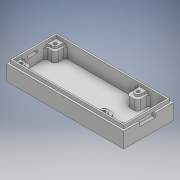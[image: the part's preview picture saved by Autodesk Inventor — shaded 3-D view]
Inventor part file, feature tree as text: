
AUTODESK INVENTOR PART (.ipt)
format: ipt  version: 2018 (Build 220112000, 112)  size: 821,760 bytes
history: native  units: mm
features: extrude x15, sketch x15, projected_geometry x6, other x1, hole x1
ambient origin geometry x8: Origin, YZ Plane, XZ Plane, XY Plane, X Axis, Y Axis, Z Axis, Center Point
bodies: Solid1 (feature_tree)
feature tree (38):
  other  "bottom"
  extrude  "walls"  Depth=3.0mm
  hole  "holes"  [1 undecoded]
  extrude  "tip"  Depth=31.0mm
  extrude  "uart"  Depth=5.0mm
  extrude  "standoffs"  Depth=2.0mm
  extrude  "finalStandoff"  Depth=2.0mm TaperAngle=0.0deg
  extrude  "forNuts"  Depth=100.0mm
  extrude  "mountHoles"  Depth=10.0mm TaperAngle=0.0deg
  extrude  "fillBeforeHoles"  Depth=10.0mm TaperAngle=0.0deg
  extrude  "jtag"  Depth=3.5mm
  extrude  "Extrusion21"  Depth=3.0mm
  extrude  "power"  Depth=2.0mm
  extrude  "powerNut"  Depth=2.0mm
  extrude  "fillBeforePowerNut"  Depth=6.0mm
  extrude  "Text"  Depth=10.0mm TaperAngle=0.0deg
  extrude  "collar"  Depth=6.5mm
  sketch  "Sketch1"  dims[d2=3.0mm d3=0.0mm d30=3.0mm]
  sketch  "Sketch5"  dims[d31=14.0mm d32=0.0mm d33=3.1mm]
  projected_geometry  "Projected Loop6"
  projected_geometry  "Projected Loop7"
  sketch  "Sketch8"  dims[d34=75.0mm d35=31.0mm]
  sketch  "Sketch9"  dims[d38=5.0mm d39=5.0mm]
  sketch  "Sketch10"  dims[d40=2.0mm d41=3.1mm]
  projected_geometry  "Projected Loop8"
  sketch  "Sketch11"  dims[d42=2.0mm d43=9.0mm d44=0.0mm]
  sketch  "Sketch12"  dims[d46=39.0mm d47=100.0mm]
  sketch  "Sketch13"  dims[d50=3.5mm d51=10.0mm d52=0.0mm]
  projected_geometry  "Projected Loop10"
  projected_geometry  "Projected Loop11"
  sketch  "Sketch14"  dims[d53=3.0mm d56=10.0mm d57=0.0mm]
  sketch  "Sketch15"  dims[d58=3.5mm d59=3.5mm]
  projected_geometry  "Projected Loop12"
  sketch  "Sketch16"  dims[d60=5.8mm d61=3.0mm]
  sketch  "Sketch17"  dims[d62=3.0mm d63=2.0mm]
  sketch  "Sketch18"  dims[d64=3.1mm d65=2.0mm]
  sketch  "Sketch19"  dims[d66=10.0mm d67=0.0mm d68=6.0mm]
  sketch  "Sketch21"  dims[d69=45.0deg d70=10.0mm d71=0.0mm d74=3.1mm d75=0.0mm d76=0.0mm d77=5.0mm d78=5.0mm d79=3.1mm d80=3.0mm d81=3.0mm d83=0.6mm d84=0.0mm d87=6.0mm d88=10.0mm d89=2.0mm d90=3.0mm d91=6.0mm d92=2.0mm d96=6.0mm d97=6.0mm d102=0.0mm d103=0.0mm d104=8.0mm d106=0.0mm d107=0.0mm d108=14.797mm d109=14.0mm d110=14.162mm d111=8.5mm d112=25.173mm d113=0.8mm d114=3.5mm d115=14.0mm d116=9.0mm d117=11.0mm d118=10.4mm d119=3.1mm d120=0.0mm d121=0.6mm d122=0.0mm d123=0.7mm d124=0.0mm d125=3.0mm d130=1.3mm d131=3.0mm d132=0.0mm d134=14.0mm d135=6.5mm d136=2.7mm d137=0.0mm]
note: 1 required parameter value undecoded (feature->parameter linkage not recoverable at this tier; creation-order binding heuristic only, values carry confidence <= 0.55)
